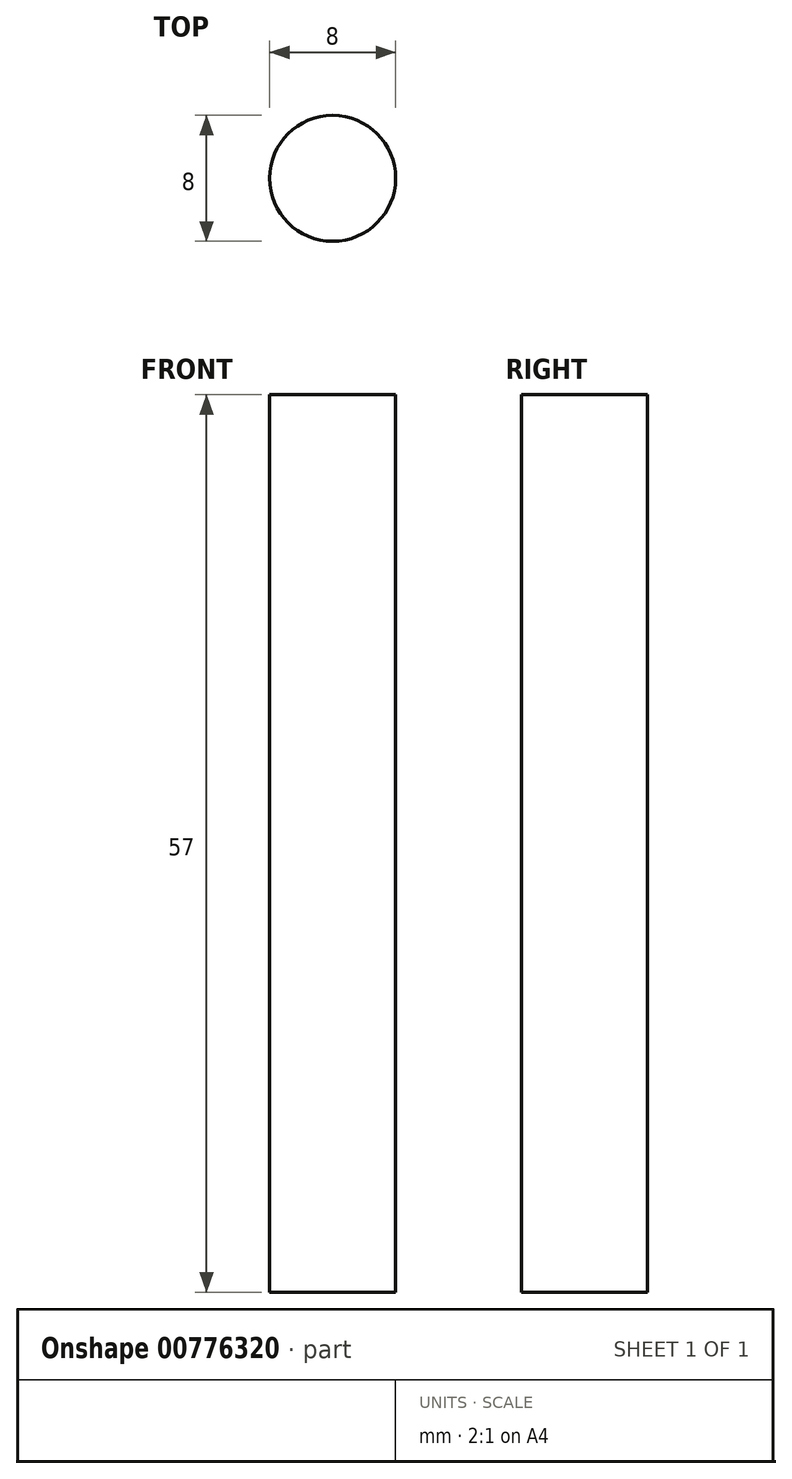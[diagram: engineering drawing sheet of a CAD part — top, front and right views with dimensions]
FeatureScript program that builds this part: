
annotation { "Feature Type Name" : "Feature", "Feature Type Description" : "" }
export const myFeature = defineFeature(function(context is Context, id is Id, definition is map)
    precondition{}
    {
        {
            var Q0;
            Q0=qCreatedBy(makeId("Top.planeOp"),FACE);
            var sketch = newSketch(context, id + "F0", { "sketchPlane" : qUnion([Q0])});
            skCircle(sketch, "E0", {"center": v(0, 0) * mm, "radius": 4 * mm});
            skSolve(sketch);
        }
        {
            var Q0;
            Q0 = qSketchRegion(id + "F0", true);
            extrude(context, id + "F1", {"entities" : qUnion([Q0]), "depth" : 57 * mm, "offsetDistance" : 25 * mm});
        }
    });
